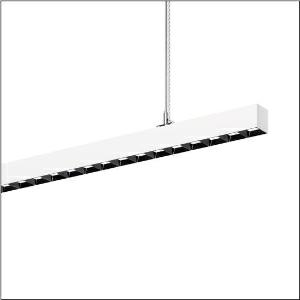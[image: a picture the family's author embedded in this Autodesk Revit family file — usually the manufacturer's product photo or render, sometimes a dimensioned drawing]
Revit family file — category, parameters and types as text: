
# Revit family: silica_r__21_51mx31tctdw_2edc
name_source: partatom
category: Lighting Fixtures
units: mm (PartAtom-declared; Revit-internal decimal feet)

## family parameters
Cut with Voids When Loaded = No
Host = Face
Light Source = No
Part Type = Normal
Room Calculation Point = No
Round Connector Dimension = Use Diameter
Shared = No

## types (1)
- --- (1 x LED, 15550 lm, 133.9 W, 6500K)
    Apparent Load = 134 VA
    CIE Flux Codes = 85 99 100 60 100
    Color Rendering = 80
    Color Temperature = 6500K
    Default Elevation = 1800 mm
    Description = Silica® 21, office luminaire, primary light control with darklight reflector, of PMMA, black, CAT 2 (L<= 3000cd/m²), light emission: direct/indirect distribution, primary light characteristic: symmetric, installation type: suspended mounting, LED, rated luminous flux: 15.550lm, luminous efficacy: 111lm/W, light colour: 8tw, colour temperature: 2700..6500K, control gear: ECG DALI, with terminal, 3+2-pole, max. 2.5mm², mains connection: 220..240V, AC, 50/60Hz, rated input power: 140.6W, luminaire housing, of aluminium, traffic white (RAL 9016), length: 3.004mm, width: 53mm, height: 53mm, protection rating (complete): IP20, insulation class (complete): insulation class I (protective earthing), certification: CE, permissible operating ambient temperature: 0..+35°C, standard: EN 50419, packaging unit: 1 piece
    Height = 53 mm
    Lamp = 1 x LED
    Lamp Light Flux = 15550 lm
    Lamp Power = 133.9 W
    Lamp count = 1
    Length = 3004 mm
    Luminous efficacy = 116 lm/W
    Manufacturer = Siteco
    ModVariant = No
    Model = 51MX31TCTDW
    Mounting Place = Ceiling
    Mounting Type = Pendant
    Number of Poles = 1
    OnlyDefault = Yes
    Power Factor = 1
    Product Name = Silica® 21
    Product group = office luminaire | ceiling pendant
    ProductGroupID = 902
    Protection Class = Protection class I
    Protection Degree = IP 20
    RLX_Detail_Level = 1
    RLX_Emergency_Light_Flux = 0 lm
    RLX_Emergency_Type = 0
    RLX_Emergency_Type_DB = No
    RlxData = <blob elided: 61101 chars, md5=9c3e1190>
    Socket = socket
    Standby Power = 0 W
    System Light Flux = 15550 lm
    System Power = 134 W
    Type Comments = individual setting
    Type Image = l_1313619.jpg
    URL = http://relux.com
    VarID = @adj_089265
    Voltage = 0 V
    Weight = 0.00 kg
    Width = 53 mm

## geometry (parser evidence)
native form markers: Blend x4, Sweep x14
no freeform markers — native parametric forms only
